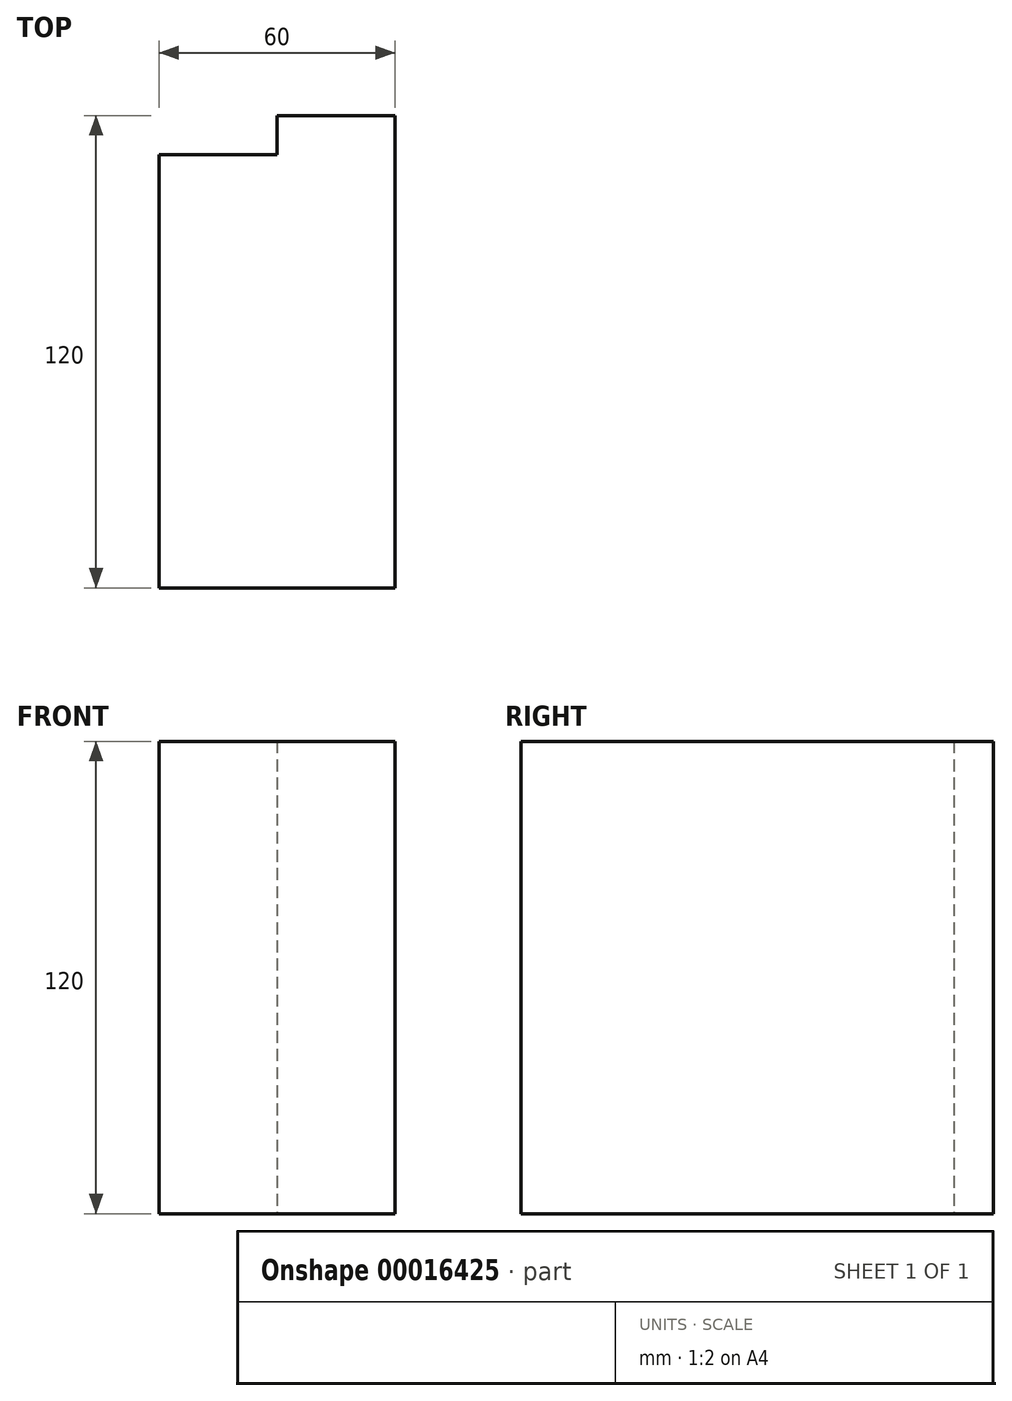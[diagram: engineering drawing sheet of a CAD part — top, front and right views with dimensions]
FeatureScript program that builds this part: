
annotation { "Feature Type Name" : "Feature", "Feature Type Description" : "" }
export const myFeature = defineFeature(function(context is Context, id is Id, definition is map)
    precondition{}
    {
        {
            var Q0;
            Q0=qCreatedBy(makeId("Top.planeOp"),FACE);
            var sketch = newSketch(context, id + "F0", { "sketchPlane" : qUnion([Q0])});
            skLineSegment(sketch, "E0.top", {"start": v(-34.29, -81.43) * mm, "end": v(25.71, -81.43) * mm});
            skLineSegment(sketch, "E0.left", {"start": v(-34.29, 28.57) * mm, "end": v(-34.29, -81.43) * mm});
            skLineSegment(sketch, "E1.bottom", {"start": v(-34.29, 28.57) * mm, "end": v(-4.29, 28.57) * mm});
            skLineSegment(sketch, "E2.right", {"start": v(-4.29, 28.57) * mm, "end": v(-4.29, 38.57) * mm});
            skLineSegment(sketch, "E2.top", {"start": v(25.71, 38.57) * mm, "end": v(-4.29, 38.57) * mm});
            skLineSegment(sketch, "E2.left", {"start": v(25.71, 28.57) * mm, "end": v(25.71, 38.57) * mm});
            skLineSegment(sketch, "E0.right", {"start": v(25.71, 28.57) * mm, "end": v(25.71, -81.43) * mm});
            skSolve(sketch);
        }
        {
            var Q0;
            Q0=makeQuery(id+"F0.imprint","IMPRINT",FACE,{"disambiguationData":[TD([[makeQuery(id+"F0.imprint","IMPRINT",EDGE,{"derivedFrom":sQuery(id+"F0.wireOp",EDGE,"E0.top")}),1.0]])]});
            var Q1;
            Q1=sQuery(id+"F0.wireOp",EDGE,"E0.top");
            var Q2;
            Q2=sQuery(id+"F0.wireOp",EDGE,"E0.left");
            var Q3;
            Q3=sQuery(id+"F0.wireOp",EDGE,"E1.bottom");
            var Q4;
            Q4=sQuery(id+"F0.wireOp",EDGE,"E2.right");
            var Q5;
            Q5=sQuery(id+"F0.wireOp",EDGE,"E2.top");
            var Q6;
            Q6=sQuery(id+"F0.wireOp",EDGE,"E2.left");
            var Q7;
            Q7=sQuery(id+"F0.wireOp",EDGE,"E0.right");
            extrude(context, id + "F1", {"entities" : qUnion([Q0]), "surfaceEntities" : qUnion([Q1, Q2, Q3, Q4, Q5, Q6, Q7]), "depth" : 120 * mm});
        }
    });
